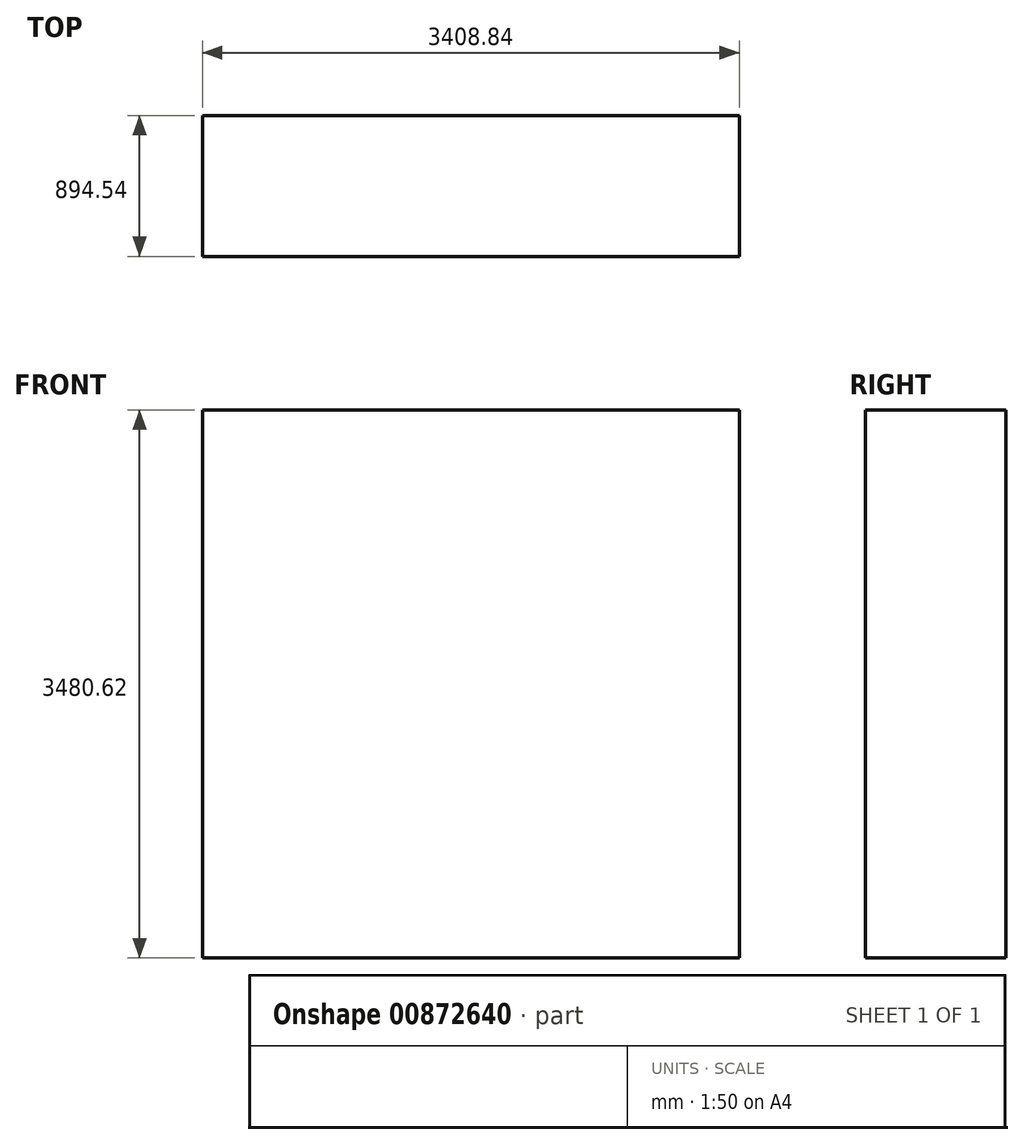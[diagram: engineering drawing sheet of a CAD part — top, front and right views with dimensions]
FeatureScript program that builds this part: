
annotation { "Feature Type Name" : "Feature", "Feature Type Description" : "" }
export const myFeature = defineFeature(function(context is Context, id is Id, definition is map)
    precondition{}
    {
        {
            var Q0;
            Q0=qCreatedBy(makeId("Front.planeOp"),FACE);
            var sketch = newSketch(context, id + "F0", { "sketchPlane" : qUnion([Q0])});
            skLineSegment(sketch, "E0.bottom", {"start": v(0, 0) * mm, "end": v(454.21, 0) * mm});
            skLineSegment(sketch, "E0.top", {"start": v(0, 781.2) * mm, "end": v(454.21, 781.2) * mm});
            skLineSegment(sketch, "E0.left", {"start": v(0, 0) * mm, "end": v(0, 781.2) * mm});
            skLineSegment(sketch, "E0.right", {"start": v(454.21, 0) * mm, "end": v(454.21, 781.2) * mm});
            skSolve(sketch);
        }
        {
            var Q0;
            Q0 = qSketchRegion(id + "F0", true);
            var sketch = newSketch(context, id + "F1", { "sketchPlane" : qUnion([Q0])});
            skLineSegment(sketch, "E1.0", {"start": v(0, 3011.2) * mm, "end": v(2207.4, 3011.2) * mm});
            skLineSegment(sketch, "E2.0", {"start": v(2200, 0) * mm, "end": v(2200, 3041.85) * mm});
            skLineSegment(sketch, "E3", {"start": v(0, 791.15) * mm, "end": v(0, 3011.2) * mm});
            skLineSegment(sketch, "E4", {"start": v(2200, 0) * mm, "end": v(475.28, 0) * mm});
            skSolve(sketch);
        }
        {
            var Q0;
            Q0=makeQuery(id+"F1.imprint","IMPRINT",FACE,{"disambiguationData":[TD([[makeQuery(id+"F1.imprint","IMPRINT",EDGE,{"derivedFrom":makeQuery(id+"F0.imprint","IMPRINT",EDGE,{"derivedFrom":sQuery(id+"F0.wireOp",EDGE,"E0.bottom")})}),1.0]])]});
            extrude(context, id + "F2", {"entities" : qUnion([Q0]), "depth" : 894.54 * mm, "offsetDistance" : 25 * mm});
        }
        {
            var Q0;
            Q0=makeQuery(id+"F2.opExtrude","SWEPT_FACE",FACE,{"disambiguationData":[OSD([sQuery(id+"F0.wireOp",EDGE,"E0.top")])]});
            var Q1;
            Q1=sQuery(id+"F0.wireOp",EDGE,"E0.left");
            extrude(context, id + "F3", {"entities" : qUnion([Q0]), "operationType" : NewBodyOperationType.ADD, "surfaceEntities" : qUnion([Q1]), "depth" : 2699.43 * mm, "offsetDistance" : 25 * mm});
        }
        {
            var Q0;
            {var subQ0=sQuery(id+"F0.wireOp",EDGE,"E0.right");Q0=makeQuery(id+"F3.boolean.opBoolean","MERGE",FACE,{"derivedFrom":[makeQuery(id+"F2.opExtrude","SWEPT_FACE",FACE,{"disambiguationData":[OSD([subQ0])]}),makeQuery(id+"F3.opExtrude","SWEPT_FACE",FACE,{"disambiguationData":[OSD([sQuery(id+"F0.wireOp",EDGE,"E0.top"),subQ0])]})]});}
            var sketch = newSketch(context, id + "F4", { "sketchPlane" : qUnion([Q0])});
            skSolve(sketch);
        }
        {
            var Q0;
            {var subQ0=sQuery(id+"F0.wireOp",EDGE,"E0.right");Q0=makeQuery(id+"F4.imprint","IMPRINT",FACE,{"disambiguationData":[TD([[makeQuery(id+"F4.imprint","IMPRINT",EDGE,{"derivedFrom":makeQuery(id+"F2.opExtrude","SWEPT_EDGE",EDGE,{"disambiguationData":[OSD([sQuery(id+"F0.wireOp",EDGE,"E0.bottom"),subQ0])]})}),1.0]])]});}
            extrude(context, id + "F5", {"entities" : qUnion([Q0]), "operationType" : NewBodyOperationType.ADD, "depth" : 2954.63 * mm, "offsetDistance" : 25 * mm});
        }
    });
